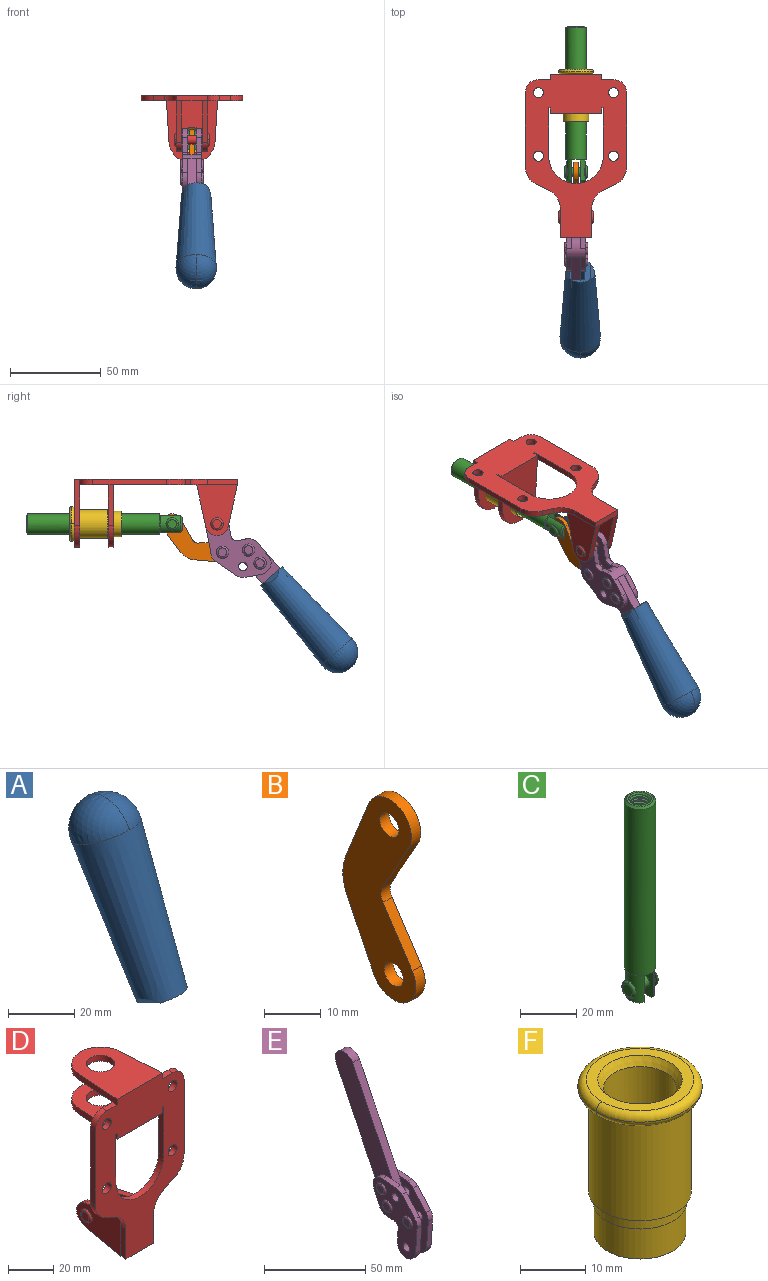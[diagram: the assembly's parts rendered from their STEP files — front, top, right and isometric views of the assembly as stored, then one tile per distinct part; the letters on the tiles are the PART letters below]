
ASSEMBLY  parts=6 mates=6
PART A: 11 faces, bbox 22.3x42.6x64.5 mm
  f0: sphere r=11.13mm, area 411.4mm2, adj f1,f8
  f1: cone r=11.11mm half-angle=3.3deg, axis (0,0.44,0.9), area 3251.8mm2, adj f0,f7,f8,f9,f10
  f2: cylinder r=6.16mm len=11.7mm, axis (1,0,0), area 89.5mm2, adj f3,f4,f5,f6
  f3: plane 60.23x36.75mm, normal (-1,0,0), area 763.6mm2, adj f2,f4,f6,f10
  f4: plane 51.37x25.05mm, normal (0,0.9,-0.44), area 264.2mm2, adj f2,f3,f5,f10
  f5: plane 60.23x36.75mm, normal (1,0,0), area 763.6mm2, adj f2,f4,f6,f10
  f6: plane 51.37x25.05mm, normal (0,-0.9,0.44), area 264.2mm2, adj f2,f3,f5,f10
  f7: plane 9.95x5.95mm, normal (0.71,-0.31,-0.64), area 25.8mm2, adj f1,f10
  f8: sphere r=11.13mm, area 411.4mm2, adj f0,f1
  f9: plane 9.95x5.95mm, normal (-0.71,-0.31,-0.64), area 25.8mm2, adj f1,f10
  f10: plane 14.27x11.38mm, normal (0,-0.44,-0.9), area 106.7mm2, adj f1,f3,f4,f5,f6,f7,f9
PART B: 12 faces, bbox 2.3x18.2x42.8 mm
  f0: cylinder r=2.4mm len=4.8mm, axis (1,0,0), area 34.9mm2, adj f4,f11
  f1: cylinder r=10.41mm len=8.47mm, axis (1,0,0), area 20.2mm2, adj f4,f9,f10,f11
  f2: cylinder r=3.05mm len=3.16mm, axis (1,0,0), area 7.7mm2, adj f4,f6,f7,f11
  f3: cylinder r=2.4mm len=4.8mm, axis (1,0,0), area 34.9mm2, adj f4,f11
  f4: plane 42.81x18.23mm, normal (-1,0,0), area 414.1mm2, adj f0,f1,f2,f3,f5,f6,f7,f8
  f5: cylinder r=5.54mm len=10.67mm, axis (1,0,0), area 41.8mm2, adj f4,f6,f10,f11
  f6: plane 11.66x6.53mm, normal (0,-0.87,-0.49), area 30.9mm2, adj f2,f4,f5,f11
  f7: plane 11.17x7.33mm, normal (0,-0.84,0.55), area 30.9mm2, adj f2,f4,f8,f11
  f8: cylinder r=5.54mm len=10.51mm, axis (1,0,0), area 41.8mm2, adj f4,f7,f9,f11
  f9: plane 13.67x6.67mm, normal (0,0.9,-0.44), area 35.1mm2, adj f1,f4,f8,f11
  f10: plane 14.1x5.7mm, normal (0,0.93,0.37), area 35.1mm2, adj f1,f4,f5,f11
  f11: plane 42.81x18.23mm, normal (1,0,0), area 414.1mm2, adj f0,f1,f2,f3,f5,f6,f7,f8
PART C: 48 faces, bbox 12.6x11.1x86.1 mm
  f0: torus R=2.41mm, axis (-1,0,0), area 15mm2, adj f30,f32,f34
  f1: torus R=2.41mm, axis (-1,0,0), area 15mm2, adj f29,f31,f33
  f2: cylinder r=5.54mm len=72.39mm, axis (0,0,1), area 2518.5mm2, adj f3,f4,f42,f43
  f3: cone r=5.54mm half-angle=45deg, axis (0,0,1), area 7.6mm2, adj f2,f5,f41
  f4: cone r=5.54mm half-angle=45deg, axis (0,0,-1), area 34.9mm2, adj f2,f39
  f5: cylinder r=5.08mm len=11.48mm, axis (0,0,1), area 108.3mm2, adj f3,f7,f8,f41
  f6: cylinder r=2.41mm len=4.83mm, axis (-1,0,0), area 71.2mm2, adj f40,f41
  f7: cylinder r=2.41mm len=4.83mm, axis (-1,0,0), area 7.6mm2, adj f5,f34
  f8: cone r=5.08mm half-angle=45deg, axis (0,0,1), area 10.6mm2, adj f5,f37,f41
  f9: cone r=3.98mm half-angle=45deg, axis (0,0,1), area 17.6mm2, adj f27,f39,f45,f46,f47
  f10: cylinder r=2.41mm len=4.83mm, axis (-1,0,0), area 7.6mm2, adj f33,f38
  f11: cylinder r=3.2mm len=6.4mm, axis (0,0,1), area 78.4mm2, adj f12,f28,f44,f45,f47
  f12: cylinder r=3.2mm len=6.4mm, axis (0,0,1), area 10.5mm2, adj f11,f13,f45,f47
  f13: cylinder r=3.2mm len=6.4mm, axis (0,0,1), area 10.5mm2, adj f12,f14,f45,f47
  f14: cylinder r=3.2mm len=6.4mm, axis (0,0,1), area 10.5mm2, adj f13,f15,f45,f47
  f15: cylinder r=3.2mm len=6.4mm, axis (0,0,1), area 10.5mm2, adj f14,f16,f45,f47
  f16: cylinder r=3.2mm len=6.4mm, axis (0,0,1), area 10.5mm2, adj f15,f17,f45,f47
  f17: cylinder r=3.2mm len=6.4mm, axis (0,0,1), area 10.5mm2, adj f16,f18,f45,f47
  f18: cylinder r=3.2mm len=6.4mm, axis (0,0,1), area 10.5mm2, adj f17,f19,f45,f47
  f19: cylinder r=3.2mm len=6.4mm, axis (0,0,1), area 10.5mm2, adj f18,f20,f45,f47
  f20: cylinder r=3.2mm len=6.4mm, axis (0,0,1), area 10.5mm2, adj f19,f21,f45,f47
  f21: cylinder r=3.2mm len=6.4mm, axis (0,0,1), area 10.5mm2, adj f20,f22,f45,f47
  f22: cylinder r=3.2mm len=6.4mm, axis (0,0,1), area 10.5mm2, adj f21,f23,f45,f47
  f23: cylinder r=3.2mm len=6.4mm, axis (0,0,1), area 10.5mm2, adj f22,f24,f45,f47
  f24: cylinder r=3.2mm len=6.4mm, axis (0,0,1), area 10.5mm2, adj f23,f25,f45,f47
  f25: cylinder r=3.2mm len=6.4mm, axis (0,0,1), area 10.5mm2, adj f24,f26,f45,f47
  f26: cylinder r=3.2mm len=6.4mm, axis (0,0,1), area 10.5mm2, adj f25,f27,f45,f47
  f27: cylinder r=3.2mm len=6.4mm, axis (0,0,1), area 7.4mm2, adj f9,f26,f45,f47
  f28: cone r=3.2mm half-angle=60deg, axis (0,0,1), area 37.2mm2, adj f11
  f29: plane 4.83x4.83mm, normal (-1,0,0), area 18.3mm2, adj f1,f31
  f30: plane 4.83x4.83mm, normal (1,0,0), area 18.3mm2, adj f0,f32
  f31: torus R=2.41mm, axis (-1,0,0), area 15mm2, adj f1,f29,f33
  f32: torus R=2.41mm, axis (-1,0,0), area 15mm2, adj f0,f30,f34
  f33: plane 6.83x6.83mm, normal (1,0,0), area 18.3mm2, adj f1,f10,f31
  f34: plane 6.83x6.83mm, normal (-1,0,0), area 18.3mm2, adj f0,f7,f32
  f35: cone r=5.08mm half-angle=45deg, axis (0,0,1), area 10.6mm2, adj f36,f38,f40
  f36: plane 7.25x1.97mm, normal (0,0,-1), area 10mm2, adj f35,f40
  f37: plane 7.25x1.97mm, normal (0,0,-1), area 10mm2, adj f8,f41
  f38: cylinder r=5.08mm len=11.48mm, axis (0,0,1), area 108.3mm2, adj f10,f35,f40,f42
  f39: plane 9.55x9.55mm, normal (0,0,1), area 22mm2, adj f4,f9
  f40: plane 12.76x10.09mm, normal (1,0,0), area 95.7mm2, adj f6,f35,f36,f38,f42,f43
  f41: plane 12.76x10.09mm, normal (-1,0,0), area 95.7mm2, adj f3,f5,f6,f8,f37,f43
  f42: cone r=5.54mm half-angle=45deg, axis (0,0,1), area 7.6mm2, adj f2,f38,f40
  f43: plane 11.07x4.7mm, normal (0,0,-1), area 50.4mm2, adj f2,f40,f41
  f44: plane 0.89x0.62mm, normal (-1,0,0), area 0.3mm2, adj f11,f45,f46,f47
  f45: bspline ~24.8x7.63mm, area 266.6mm2, adj f9,f11,f12,f13,f14,f15,f16,f17
  f46: bspline ~24.87x7.63mm, area 73.6mm2, adj f9,f44,f45,f47
  f47: bspline ~24.98x7.63mm, area 272.5mm2, adj f9,f11,f12,f13,f14,f15,f16,f17
PART D: 55 faces, bbox 55.7x37.4x89.8 mm
  f0: torus R=2.41mm, axis (-1,0,0), area 15mm2, adj f11,f15,f25
  f1: torus R=2.41mm, axis (-1,0,0), area 15mm2, adj f10,f12,f22
  f2: cylinder r=2.78mm len=5.56mm, axis (0,-1,0), area 54.2mm2, adj f30,f54
  f3: cylinder r=14.99mm len=29.97mm, axis (0,-1,0), area 145.9mm2, adj f30,f49,f53,f54
  f4: cylinder r=2.78mm len=5.56mm, axis (0,-1,0), area 54.2mm2, adj f30,f54
  f5: cylinder r=2.78mm len=5.56mm, axis (0,-1,0), area 54.2mm2, adj f30,f54
  f6: cylinder r=2.78mm len=5.56mm, axis (0,-1,0), area 54.2mm2, adj f30,f54
  f7: cylinder r=6.35mm len=12.7mm, axis (0,0,1), area 123.6mm2, adj f27,f51
  f8: cylinder r=6.35mm len=12.7mm, axis (0,0,-1), area 124.7mm2, adj f21,f35
  f9: cylinder r=2.41mm len=11.18mm, axis (-1,0,0), area 169.4mm2, adj f16,f19
  f10: plane 4.83x4.83mm, normal (1,0,0), area 18.3mm2, adj f1,f12
  f11: plane 4.83x4.83mm, normal (-1,0,0), area 18.3mm2, adj f0,f15
  f12: torus R=2.41mm, axis (-1,0,0), area 15mm2, adj f1,f10,f22
  f13: cylinder r=6.35mm len=12.41mm, axis (1,0,0), area 53.4mm2, adj f18,f19,f22,f23
  f14: cylinder r=6.35mm len=12.41mm, axis (-1,0,0), area 53.4mm2, adj f16,f17,f24,f25
  f15: torus R=2.41mm, axis (-1,0,0), area 15mm2, adj f0,f11,f25
  f16: plane 27.86x22.35mm, normal (1,0,0), area 425.4mm2, adj f9,f14,f17,f24,f30
  f17: plane 22.86x4.97mm, normal (0,0.21,0.98), area 72.5mm2, adj f14,f16,f25,f30
  f18: plane 22.86x4.97mm, normal (0,0.21,0.98), area 72.5mm2, adj f13,f19,f22,f30
  f19: plane 27.86x22.35mm, normal (-1,0,0), area 425.4mm2, adj f9,f13,f18,f23,f30
  f20: cylinder r=12.7mm len=25.35mm, axis (0,0,-1), area 119.8mm2, adj f21,f34,f35,f36
  f21: plane 34.21x28.07mm, normal (0,0,-1), area 702.4mm2, adj f8,f20,f30,f34,f36
  f22: plane 27.96x22.45mm, normal (1,0,0), area 407.2mm2, adj f1,f12,f13,f18,f23,f30,f42,f43
  f23: plane 22.86x4.97mm, normal (0,0.21,-0.98), area 72.5mm2, adj f13,f19,f22,f44
  f24: plane 22.86x4.97mm, normal (0,0.21,-0.98), area 72.5mm2, adj f14,f16,f25,f44
  f25: plane 27.86x22.35mm, normal (-1,0,0), area 407.1mm2, adj f0,f14,f15,f17,f24,f30,f45,f46
  f26: plane 3.1x0.95mm, normal (0,0,-1), area 2.7mm2, adj f30,f49,f50,f54
  f27: plane 34.21x28.07mm, normal (0,0,1), area 702.4mm2, adj f7,f28,f30,f50,f52
  f28: cylinder r=12.7mm len=25.35mm, axis (0,0,1), area 118.8mm2, adj f27,f50,f51,f52
  f29: plane 3.1x0.95mm, normal (0,0,-1), area 2.7mm2, adj f30,f52,f53,f54
  f30: plane 86.54x55.63mm, normal (0,1,0), area 2362.9mm2, adj f2,f3,f4,f5,f6,f16,f17,f18
  f31: plane 40.56x3.1mm, normal (-1,0,0), area 125.7mm2, adj f30,f32,f48,f54
  f32: cylinder r=7.11mm len=7.11mm, axis (0,-1,0), area 34.6mm2, adj f30,f31,f33,f54
  f33: plane 6.67x3.1mm, normal (0,0,1), area 20.4mm2, adj f30,f32,f34,f54
  f34: plane 25.39x3.13mm, normal (-1,0.06,0), area 79.5mm2, adj f20,f21,f33,f35,f54
  f35: plane 37.31x28.45mm, normal (0,0,1), area 789.9mm2, adj f8,f20,f34,f36,f54
  f36: plane 25.39x3.13mm, normal (1,0.06,0), area 79.5mm2, adj f20,f21,f35,f37,f54
  f37: plane 6.67x3.1mm, normal (0,0,1), area 20.4mm2, adj f30,f36,f38,f54
  f38: cylinder r=7.11mm len=7.11mm, axis (0,-1,0), area 34.6mm2, adj f30,f37,f39,f54
  f39: plane 40.56x3.1mm, normal (1,0,0), area 125.7mm2, adj f30,f38,f40,f54
  f40: cylinder r=11.18mm len=10.16mm, axis (0,-1,0), area 39.5mm2, adj f30,f39,f41,f54
  f41: plane 6.09x3.1mm, normal (0.42,0,-0.91), area 20.8mm2, adj f30,f40,f42,f54
  f42: cylinder r=11.18mm len=9.41mm, axis (0,-1,0), area 37.2mm2, adj f22,f30,f41,f43,f54
  f43: plane 16.5x3.1mm, normal (1,0,0), area 51.1mm2, adj f22,f42,f44,f54
  f44: plane 17.37x3.1mm, normal (0,0,-1), area 53.8mm2, adj f23,f24,f30,f43,f45,f54
  f45: plane 16.5x3.1mm, normal (-1,0,0), area 51.1mm2, adj f25,f44,f46,f54
  f46: cylinder r=11.18mm len=9.41mm, axis (0,-1,0), area 37.2mm2, adj f25,f30,f45,f47,f54
  f47: plane 6.09x3.1mm, normal (-0.42,0,-0.91), area 20.8mm2, adj f30,f46,f48,f54
  f48: cylinder r=11.18mm len=10.16mm, axis (0,-1,0), area 39.5mm2, adj f30,f31,f47,f54
  f49: plane 26.54x3.1mm, normal (-1,0,0), area 82.3mm2, adj f3,f26,f30,f54
  f50: plane 25.39x3.1mm, normal (1,0.06,0), area 78.8mm2, adj f26,f27,f28,f51,f54
  f51: plane 37.31x28.45mm, normal (0,0,-1), area 789.9mm2, adj f7,f28,f50,f52,f54
  f52: plane 25.39x3.1mm, normal (-1,0.06,0), area 78.8mm2, adj f27,f28,f29,f51,f54
  f53: plane 26.54x3.1mm, normal (1,0,0), area 82.3mm2, adj f3,f29,f30,f54
  f54: plane 89.66x55.63mm, normal (0,-1,0), area 2678.5mm2, adj f2,f3,f4,f5,f6,f26,f29,f31
PART E: 59 faces, bbox 12.9x60.2x99.6 mm
  f0: torus R=2.39mm, axis (-1,0,0), area 14.9mm2, adj f20,f43,f51
  f1: torus R=2.39mm, axis (-1,0,0), area 14.9mm2, adj f19,f42,f51
  f2: torus R=2.39mm, axis (-1,0,0), area 14.9mm2, adj f18,f35,f51
  f3: torus R=2.39mm, axis (-1,0,0), area 14.9mm2, adj f14,f17,f23
  f4: torus R=2.39mm, axis (-1,0,0), area 14.9mm2, adj f13,f16,f23
  f5: torus R=2.39mm, axis (-1,0,0), area 14.9mm2, adj f12,f15,f23
  f6: cylinder r=2.39mm len=4.78mm, axis (1,0,0), area 46.5mm2, adj f48,f50,f51
  f7: cylinder r=2.39mm len=4.78mm, axis (1,0,0), area 46.5mm2, adj f50,f51
  f8: cylinder r=6.35mm len=12.68mm, axis (1,0,0), area 61.8mm2, adj f38,f39,f50,f51
  f9: cylinder r=2.39mm len=4.78mm, axis (-1,0,0), area 70.5mm2, adj f46,f50
  f10: cylinder r=2.39mm len=4.78mm, axis (-1,0,0), area 46.5mm2, adj f23,f45,f46
  f11: cylinder r=2.39mm len=4.78mm, axis (-1,0,0), area 46.5mm2, adj f23,f46
  f12: plane 4.78x4.78mm, normal (1,0,0), area 17.9mm2, adj f5,f15
  f13: plane 4.78x4.78mm, normal (1,0,0), area 17.9mm2, adj f4,f16
  f14: plane 4.78x4.78mm, normal (1,0,0), area 17.9mm2, adj f3,f17
  f15: torus R=2.39mm, axis (-1,0,0), area 14.9mm2, adj f5,f12,f23
  f16: torus R=2.39mm, axis (-1,0,0), area 14.9mm2, adj f4,f13,f23
  f17: torus R=2.39mm, axis (-1,0,0), area 14.9mm2, adj f3,f14,f23
  f18: plane 4.78x4.78mm, normal (-1,0,0), area 17.9mm2, adj f2,f35
  f19: plane 4.78x4.78mm, normal (-1,0,0), area 17.9mm2, adj f1,f42
  f20: plane 4.78x4.78mm, normal (-1,0,0), area 17.9mm2, adj f0,f43
  f21: plane 2.26x0.2mm, normal (1,0,0), area 0.2mm2, adj f31,f44
  f22: plane 2.26x0.2mm, normal (-1,0,0), area 0.2mm2, adj f41,f44
  f23: plane 39.37x30.77mm, normal (1,0,0), area 565.5mm2, adj f3,f4,f5,f10,f11,f15,f16,f17
  f24: cylinder r=6.1mm len=4.15mm, axis (-1,0,0), area 14.7mm2, adj f23,f25,f32,f46
  f25: plane 10.25x9.01mm, normal (0,-0.75,0.66), area 42.3mm2, adj f23,f24,f26,f46
  f26: cylinder r=6.35mm len=4.64mm, axis (-1,0,0), area 15.6mm2, adj f23,f25,f27,f46
  f27: plane 15.84x3.1mm, normal (0,-1,-0.07), area 49.2mm2, adj f23,f26,f28,f46
  f28: cylinder r=6.35mm len=12.68mm, axis (-1,0,0), area 61.8mm2, adj f23,f27,f29,f46
  f29: plane 8.11x3.1mm, normal (0,1,0.07), area 25.2mm2, adj f23,f28,f30,f46
  f30: cylinder r=3.05mm len=3.25mm, axis (-1,0,0), area 14.8mm2, adj f23,f29,f31,f46
  f31: plane 5.99x3.1mm, normal (0,0.07,-1), area 18.6mm2, adj f21,f23,f30,f44,f46
  f32: plane 9.5x3.1mm, normal (0,-0.07,1), area 29.5mm2, adj f23,f24,f33,f46,f47
  f33: cylinder r=6.1mm len=8.63mm, axis (-1,0,0), area 39.1mm2, adj f23,f32,f34,f47
  f34: plane 8.65x3.96mm, normal (0,0.91,-0.42), area 29.5mm2, adj f23,f33,f44,f47
  f35: torus R=2.39mm, axis (-1,0,0), area 14.9mm2, adj f2,f18,f51
  f36: plane 10.25x9.01mm, normal (0,-0.75,0.66), area 42.3mm2, adj f37,f49,f50,f51
  f37: cylinder r=6.35mm len=4.64mm, axis (1,0,0), area 15.6mm2, adj f36,f38,f50,f51
  f38: plane 15.84x3.1mm, normal (0,-1,-0.07), area 49.2mm2, adj f8,f37,f50,f51
  f39: plane 8.11x3.1mm, normal (0,1,0.07), area 25.2mm2, adj f8,f40,f50,f51
  f40: cylinder r=3.05mm len=3.25mm, axis (1,0,0), area 14.8mm2, adj f39,f41,f50,f51
  f41: plane 5.99x3.1mm, normal (0,0.07,-1), area 18.6mm2, adj f22,f40,f44,f50,f51
  f42: torus R=2.39mm, axis (-1,0,0), area 14.9mm2, adj f1,f19,f51
  f43: torus R=2.39mm, axis (-1,0,0), area 14.9mm2, adj f0,f20,f51
  f44: cylinder r=6.35mm len=12.12mm, axis (-1,0,0), area 128.9mm2, adj f21,f22,f23,f31,f34,f41,f46,f47
  f45: plane 2.65x1.35mm, normal (1,0,0), area 1mm2, adj f10,f55
  f46: plane 39.08x20.42mm, normal (-1,0,0), area 412.5mm2, adj f9,f10,f11,f24,f25,f26,f27,f28
  f47: plane 77.62x39.82mm, normal (1,0,0), area 850mm2, adj f32,f33,f34,f44,f53,f54,f55
  f48: plane 2.65x1.35mm, normal (-1,0,0), area 1mm2, adj f6,f55
  f49: cylinder r=6.1mm len=4.15mm, axis (1,0,0), area 14.7mm2, adj f36,f50,f51,f56
  f50: plane 39.08x20.42mm, normal (1,0,0), area 412.5mm2, adj f6,f7,f8,f9,f36,f37,f38,f39
  f51: plane 39.37x30.77mm, normal (-1,0,0), area 565.5mm2, adj f0,f1,f2,f6,f7,f8,f35,f36
  f52: plane 8.65x3.96mm, normal (0,0.91,-0.42), area 29.5mm2, adj f44,f51,f57,f58
  f53: plane 68.49x33.4mm, normal (0,0.9,-0.44), area 358.1mm2, adj f44,f47,f54,f58
  f54: cylinder r=6.35mm len=12.06mm, axis (1,0,0), area 93.7mm2, adj f47,f53,f55,f58
  f55: plane 68.49x33.4mm, normal (0,-0.9,0.44), area 358.1mm2, adj f44,f45,f46,f47,f48,f50,f54,f58
  f56: plane 9.5x3.1mm, normal (0,-0.07,1), area 29.5mm2, adj f49,f50,f51,f57,f58
  f57: cylinder r=6.1mm len=8.63mm, axis (1,0,0), area 39.1mm2, adj f51,f52,f56,f58
  f58: plane 77.62x39.82mm, normal (-1,0,0), area 850mm2, adj f44,f52,f53,f54,f55,f56,f57
PART F: 15 faces, bbox 20.6x20.6x28.7 mm
  f0: torus R=8.26mm, axis (0,0,1), area 56.8mm2, adj f1,f10,f12
  f1: torus R=8.26mm, axis (0,0,1), area 56.8mm2, adj f0,f6,f13
  f2: cylinder r=5.59mm len=25.91mm, axis (0,0,1), area 909.6mm2, adj f3,f4
  f3: cone r=6.86mm half-angle=45deg, axis (0,0,-1), area 70.2mm2, adj f2,f14
  f4: cone r=6.47mm half-angle=30deg, axis (0,0,1), area 66.7mm2, adj f2,f13
  f5: cylinder r=7.04mm len=14.07mm, axis (0,0,1), area 252.6mm2, adj f11,f14
  f6: torus R=8.26mm, axis (0,0,1), area 56.8mm2, adj f1,f12,f13
  f7: cylinder r=7.16mm len=14.33mm, axis (0,0,1), area 91.5mm2, adj f9,f11
  f8: cylinder r=7.86mm len=18.42mm, axis (0,0,1), area 909.6mm2, adj f9,f10
  f9: plane 15.72x15.72mm, normal (0,0,-1), area 33mm2, adj f7,f8
  f10: plane 16.51x16.51mm, normal (0,0,-1), area 19.9mm2, adj f0,f8,f12
  f11: plane 14.33x14.33mm, normal (0,0,-1), area 5.7mm2, adj f5,f7
  f12: torus R=8.26mm, axis (0,0,1), area 56.8mm2, adj f0,f6,f10
  f13: plane 16.51x16.51mm, normal (0,0,1), area 82.7mm2, adj f1,f4,f6
  f14: plane 14.07x14.07mm, normal (0,0,-1), area 7.8mm2, adj f3,f5
PLACE A rot(axis=(1,0,0),165deg) t=(2.31,-25.77,-61.98)mm
PLACE B rot(axis=(-1,0,0),58.6deg) t=(0,-42.63,-11.66)mm
PLACE C rot(axis=(-1,0,0),90deg) t=(0,-32.07,0)mm
PLACE D rot(axis=(-1,0,0),90deg) t=(0,-9.14,0)mm fixed
PLACE E rot(axis=(1,0,0),165deg) t=(0,-25.77,-61.98)mm
PLACE F rot(axis=(-1,0,0),90deg) t=(0,-9.14,0)mm
MATE revolute B.f5 <-> C.f6  axis (1,0,0) through (0,-16.6,-24.61)mm
MATE fastened A.f2 <-> E.f54  axis (1,0,0) through (0,-108.56,-96.5)mm
MATE slider C.f2 <-> F.f2  axis (0,1,0) through (0,26.71,-24.61)mm
MATE revolute B.f3 <-> E.f4  axis (1,0,0) through (0,-44.26,-40.2)mm
MATE revolute E.f7 <-> D.f0  axis (1,0,0) through (0,-41.23,-24.61)mm
MATE fastened F.f2 <-> D.f7  axis (0,-1,0) through (0,37.25,-24.61)mm
